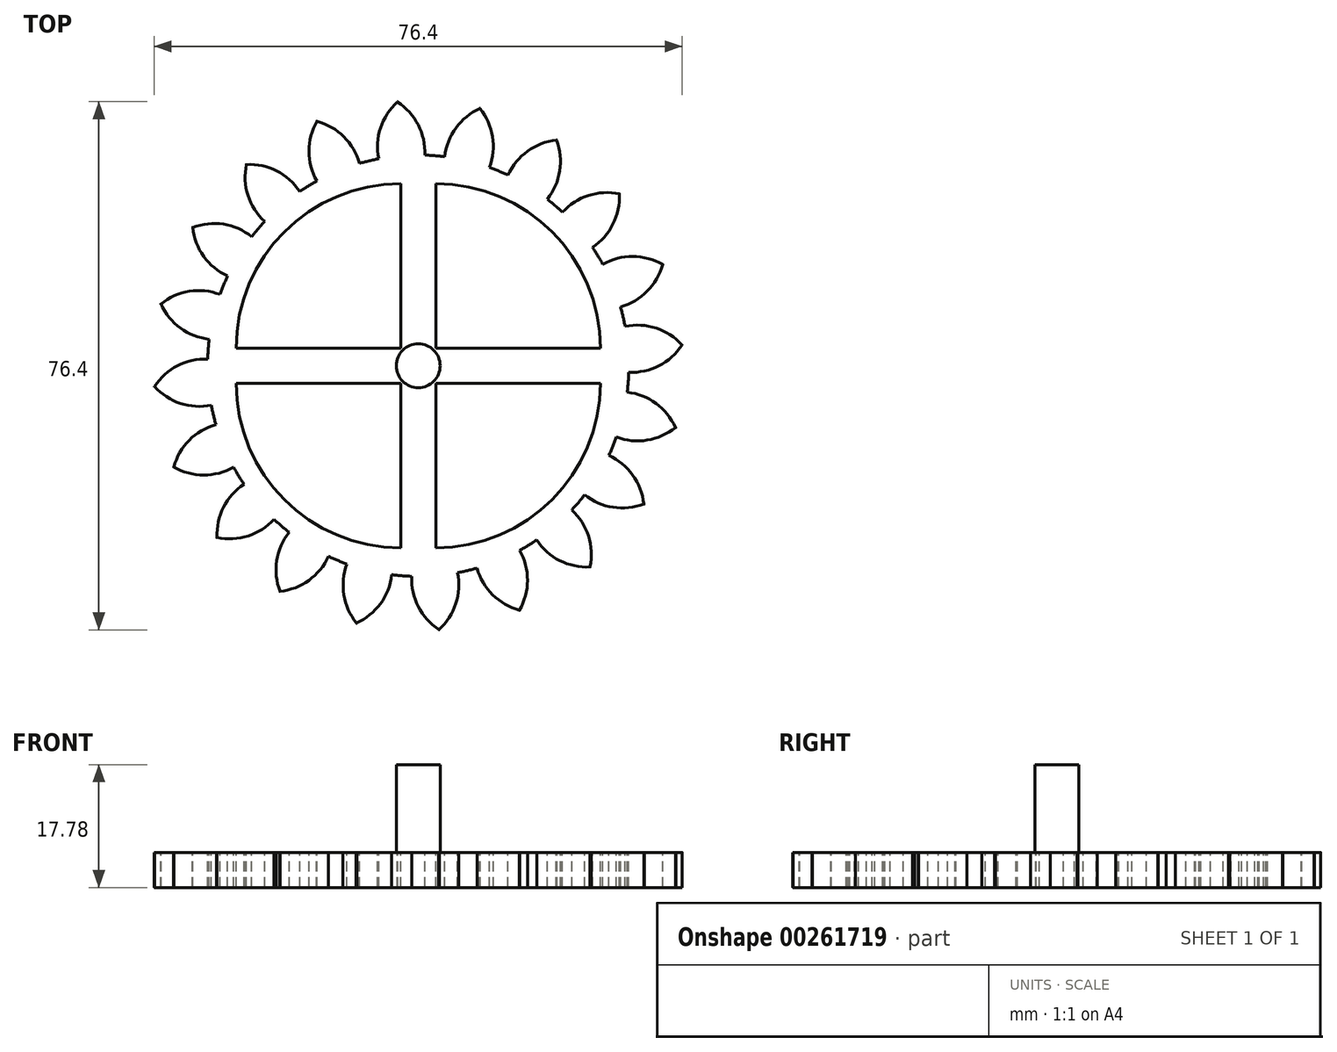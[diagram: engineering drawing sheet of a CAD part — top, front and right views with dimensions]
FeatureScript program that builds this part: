
annotation { "Feature Type Name" : "Feature", "Feature Type Description" : "" }
export const myFeature = defineFeature(function(context is Context, id is Id, definition is map)
    precondition{}
    {
        {
            var Q0;
            Q0=qCreatedBy(makeId("Top.planeOp"),FACE);
            var sketch = newSketch(context, id + "F0", { "sketchPlane" : qUnion([Q0])});
            skCircle(sketch, "E0", {"center": v(0, 0) * mm, "radius": 30.48 * mm});
            skSolve(sketch);
        }
        {
            var Q0;
            Q0=qSketchRegion(id+"F0",true);
            extrude(context, id + "F1", {"entities" : qUnion([Q0]), "depth" : 5.08 * mm});
        }
        {
            var Q0;
            Q0=makeQuery(id+"F1.opExtrude","CAP_FACE",FACE,{"disambiguationData":[OSD([sQuery(id+"F0.wireOp",EDGE,"E0")])],"isStart":false});
            var sketch = newSketch(context, id + "F2", { "sketchPlane" : qUnion([Q0])});
            skCircle(sketch, "E1", {"center": v(0, 0) * mm, "radius": 38.31 * mm, "construction": true});
            skCircle(sketch, "E2", {"center": v(0, 0) * mm, "radius": 34.83 * mm, "construction": true});
            skCircle(sketch, "E3", {"center": v(0, 0) * mm, "radius": 30.48 * mm, "construction": true});
            skLineSegment(sketch, "E4", {"start": v(0, 0) * mm, "end": v(0, 56.9) * mm, "construction": true});
            skLineSegment(sketch, "E5", {"start": v(0, 0) * mm, "end": v(-4.62, 58.65) * mm, "construction": true});
            skLineSegment(sketch, "E6", {"start": v(0, 34.83) * mm, "end": v(-65.71, 34.83) * mm, "construction": true});
            skLineSegment(sketch, "E7", {"start": v(0, 34.83) * mm, "end": v(-58.85, 8.63) * mm, "construction": true});
            skCircle(sketch, "E8", {"center": v(0, 34.83) * mm, "radius": 8.7 * mm, "construction": true});
            skCircle(sketch, "E9", {"center": v(0, 0) * mm, "radius": 31.82 * mm, "construction": true});
            skCircle(sketch, "E10", {"center": v(-7.75, 30.86) * mm, "radius": 8.7 * mm, "construction": true});
            skArc(sketch, "E11", {"start": v(0.95, 30.46) * mm, "mid": v(-0.02, 34.86) * mm, "end": v(-3.05, 38.2) * mm});
            skArc(sketch, "E12.MirrorCS", {"start": v(-5.7, 29.94) * mm, "mid": v(-5.44, 34.44) * mm, "end": v(-2.96, 38.2) * mm});
            skLineSegment(sketch, "E13", {"start": v(-3.05, 38.2) * mm, "end": v(-2.96, 38.2) * mm});
            skLineSegment(sketch, "E14", {"start": v(-5.7, 29.94) * mm, "end": v(0.95, 30.46) * mm});
            skSolve(sketch);
        }
        {
            var Q0;
            Q0=qSketchRegion(id+"F2",true);
            var Q1;
            Q1=makeQuery(id+"F1.opExtrude","CAP_FACE",FACE,{"disambiguationData":[OSD([sQuery(id+"F0.wireOp",EDGE,"E0")])],"isStart":true});
            extrude(context, id + "F3", {"entities" : qUnion([Q0]), "endBound" : BoundingType.UP_TO_SURFACE, "oppositeDirection" : true, "endBoundEntityFace" : qUnion([Q1]), "depth" : 25.4 * mm});
        }
        {
            var Q0;
            {var subQ0=sQuery(id+"F2.wireOp",EDGE,"E12.MirrorCS");var subQ1=sQuery(id+"F2.wireOp",EDGE,"E11");Q0=qUnion([makeQuery(id+"F3.opExtrude","SWEPT_BODY",BODY,{"disambiguationData":[OSD([subQ1,subQ0,sQuery(id+"F2.wireOp",EDGE,"E14")])]}),makeQuery(id+"F3.opExtrude","SWEPT_BODY",BODY,{"disambiguationData":[OSD([subQ1,subQ0,sQuery(id+"F2.wireOp",EDGE,"E13")])]})]);}
            var Q1;
            Q1=makeQuery(id+"F1.opExtrude","CAP_EDGE",EDGE,{"disambiguationData":[OSD([sQuery(id+"F0.wireOp",EDGE,"E0")])],"isStart":false});
            circularPattern(context, id + "F4", {"operationType" : NewBodyOperationType.ADD, "entities" : qUnion([Q0]), "axis" : qUnion([Q1]), "angle" : 360 * degree, "instanceCount" : 20, "equalSpace" : true});
        }
        {
            var Q0;
            {var subQ0=makeQuery(id+"F3.opExtrude","CAP_FACE",FACE,{"disambiguationData":[OSD([sQuery(id+"F2.wireOp",EDGE,"E11"),sQuery(id+"F2.wireOp",EDGE,"E12.MirrorCS"),sQuery(id+"F2.wireOp",EDGE,"E14")])],"isStart":true});Q0=makeQuery(id+"F4.boolean.opBoolean","MERGE",FACE,{"derivedFrom":[makeQuery(id+"F1.opExtrude","CAP_FACE",FACE,{"disambiguationData":[OSD([sQuery(id+"F0.wireOp",EDGE,"E0")])],"isStart":false}),subQ0,makeQuery(id+"F4.opPattern","COPY",FACE,{"derivedFrom":subQ0,"instanceName":"1"}),makeQuery(id+"F4.opPattern","COPY",FACE,{"derivedFrom":subQ0,"instanceName":"2"}),makeQuery(id+"F4.opPattern","COPY",FACE,{"derivedFrom":subQ0,"instanceName":"3"}),makeQuery(id+"F4.opPattern","COPY",FACE,{"derivedFrom":subQ0,"instanceName":"4"}),makeQuery(id+"F4.opPattern","COPY",FACE,{"derivedFrom":subQ0,"instanceName":"5"}),makeQuery(id+"F4.opPattern","COPY",FACE,{"derivedFrom":subQ0,"instanceName":"6"}),makeQuery(id+"F4.opPattern","COPY",FACE,{"derivedFrom":subQ0,"instanceName":"7"}),makeQuery(id+"F4.opPattern","COPY",FACE,{"derivedFrom":subQ0,"instanceName":"8"}),makeQuery(id+"F4.opPattern","COPY",FACE,{"derivedFrom":subQ0,"instanceName":"9"}),makeQuery(id+"F4.opPattern","COPY",FACE,{"derivedFrom":subQ0,"instanceName":"10"}),makeQuery(id+"F4.opPattern","COPY",FACE,{"derivedFrom":subQ0,"instanceName":"11"}),makeQuery(id+"F4.opPattern","COPY",FACE,{"derivedFrom":subQ0,"instanceName":"12"}),makeQuery(id+"F4.opPattern","COPY",FACE,{"derivedFrom":subQ0,"instanceName":"13"}),makeQuery(id+"F4.opPattern","COPY",FACE,{"derivedFrom":subQ0,"instanceName":"14"}),makeQuery(id+"F4.opPattern","COPY",FACE,{"derivedFrom":subQ0,"instanceName":"15"}),makeQuery(id+"F4.opPattern","COPY",FACE,{"derivedFrom":subQ0,"instanceName":"16"}),makeQuery(id+"F4.opPattern","COPY",FACE,{"derivedFrom":subQ0,"instanceName":"17"}),makeQuery(id+"F4.opPattern","COPY",FACE,{"derivedFrom":subQ0,"instanceName":"18"}),makeQuery(id+"F4.opPattern","COPY",FACE,{"derivedFrom":subQ0,"instanceName":"19"})]});}
            var sketch = newSketch(context, id + "F5", { "sketchPlane" : qUnion([Q0])});
            skLineSegment(sketch, "E15", {"start": v(-2.54, 2.54) * mm, "end": v(-26.34, 2.54) * mm});
            skLineSegment(sketch, "E16", {"start": v(-2.54, 2.54) * mm, "end": v(-2.54, 26.34) * mm});
            skArc(sketch, "E17", {"start": v(-2.54, 26.34) * mm, "mid": v(-19.37, 19.37) * mm, "end": v(-26.34, 2.54) * mm});
            skArc(sketch, "E18.1.0", {"start": v(-26.34, -2.54) * mm, "mid": v(-19.37, -19.37) * mm, "end": v(-2.54, -26.34) * mm});
            skLineSegment(sketch, "E18.1.1", {"start": v(-2.54, -2.54) * mm, "end": v(-26.34, -2.54) * mm});
            skLineSegment(sketch, "E18.1.2", {"start": v(-2.54, -2.54) * mm, "end": v(-2.54, -26.34) * mm});
            skArc(sketch, "E18.2.0", {"start": v(2.54, -26.34) * mm, "mid": v(19.37, -19.37) * mm, "end": v(26.34, -2.54) * mm});
            skLineSegment(sketch, "E18.2.1", {"start": v(2.54, -2.54) * mm, "end": v(2.54, -26.34) * mm});
            skLineSegment(sketch, "E18.2.2", {"start": v(2.54, -2.54) * mm, "end": v(26.34, -2.54) * mm});
            skArc(sketch, "E18.3.0", {"start": v(26.34, 2.54) * mm, "mid": v(19.37, 19.37) * mm, "end": v(2.54, 26.34) * mm});
            skLineSegment(sketch, "E18.3.1", {"start": v(2.54, 2.54) * mm, "end": v(26.34, 2.54) * mm});
            skLineSegment(sketch, "E18.3.2", {"start": v(2.54, 2.54) * mm, "end": v(2.54, 26.34) * mm});
            skPoint(sketch, "E18.center", {"position": v(0, 0) * mm});
            skSolve(sketch);
        }
        {
            var Q0;
            Q0=qSketchRegion(id+"F5",true);
            extrude(context, id + "F6", {"entities" : qUnion([Q0]), "operationType" : NewBodyOperationType.REMOVE, "endBound" : BoundingType.THROUGH_ALL, "oppositeDirection" : true, "depth" : 25.4 * mm});
        }
        {
            var Q0;
            {var subQ0=makeQuery(id+"F3.opExtrude","CAP_FACE",FACE,{"disambiguationData":[OSD([sQuery(id+"F2.wireOp",EDGE,"E11"),sQuery(id+"F2.wireOp",EDGE,"E12.MirrorCS"),sQuery(id+"F2.wireOp",EDGE,"E14")])],"isStart":true});Q0=makeQuery(id+"F4.boolean.opBoolean","MERGE",FACE,{"derivedFrom":[makeQuery(id+"F1.opExtrude","CAP_FACE",FACE,{"disambiguationData":[OSD([sQuery(id+"F0.wireOp",EDGE,"E0")])],"isStart":false}),subQ0,makeQuery(id+"F4.opPattern","COPY",FACE,{"derivedFrom":subQ0,"instanceName":"1"}),makeQuery(id+"F4.opPattern","COPY",FACE,{"derivedFrom":subQ0,"instanceName":"2"}),makeQuery(id+"F4.opPattern","COPY",FACE,{"derivedFrom":subQ0,"instanceName":"3"}),makeQuery(id+"F4.opPattern","COPY",FACE,{"derivedFrom":subQ0,"instanceName":"4"}),makeQuery(id+"F4.opPattern","COPY",FACE,{"derivedFrom":subQ0,"instanceName":"5"}),makeQuery(id+"F4.opPattern","COPY",FACE,{"derivedFrom":subQ0,"instanceName":"6"}),makeQuery(id+"F4.opPattern","COPY",FACE,{"derivedFrom":subQ0,"instanceName":"7"}),makeQuery(id+"F4.opPattern","COPY",FACE,{"derivedFrom":subQ0,"instanceName":"8"}),makeQuery(id+"F4.opPattern","COPY",FACE,{"derivedFrom":subQ0,"instanceName":"9"}),makeQuery(id+"F4.opPattern","COPY",FACE,{"derivedFrom":subQ0,"instanceName":"10"}),makeQuery(id+"F4.opPattern","COPY",FACE,{"derivedFrom":subQ0,"instanceName":"11"}),makeQuery(id+"F4.opPattern","COPY",FACE,{"derivedFrom":subQ0,"instanceName":"12"}),makeQuery(id+"F4.opPattern","COPY",FACE,{"derivedFrom":subQ0,"instanceName":"13"}),makeQuery(id+"F4.opPattern","COPY",FACE,{"derivedFrom":subQ0,"instanceName":"14"}),makeQuery(id+"F4.opPattern","COPY",FACE,{"derivedFrom":subQ0,"instanceName":"15"}),makeQuery(id+"F4.opPattern","COPY",FACE,{"derivedFrom":subQ0,"instanceName":"16"}),makeQuery(id+"F4.opPattern","COPY",FACE,{"derivedFrom":subQ0,"instanceName":"17"}),makeQuery(id+"F4.opPattern","COPY",FACE,{"derivedFrom":subQ0,"instanceName":"18"}),makeQuery(id+"F4.opPattern","COPY",FACE,{"derivedFrom":subQ0,"instanceName":"19"})]});}
            var sketch = newSketch(context, id + "F7", { "sketchPlane" : qUnion([Q0])});
            skCircle(sketch, "E19", {"center": v(0, 0) * mm, "radius": 3.18 * mm});
            skSolve(sketch);
        }
        {
            var Q0;
            Q0=qSketchRegion(id+"F7",true);
            extrude(context, id + "F8", {"entities" : qUnion([Q0]), "operationType" : NewBodyOperationType.ADD, "depth" : 12.7 * mm});
        }
    });
